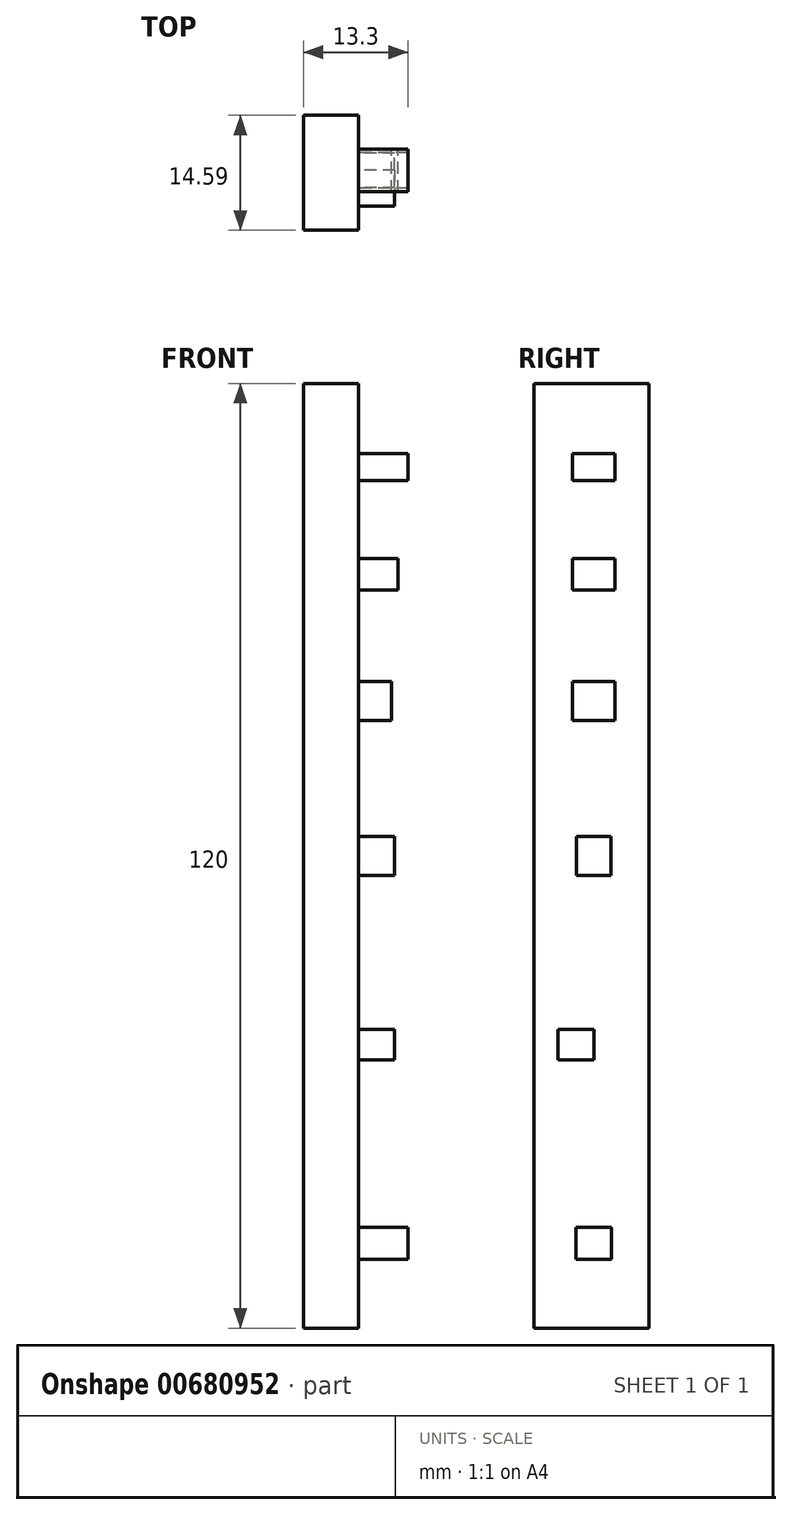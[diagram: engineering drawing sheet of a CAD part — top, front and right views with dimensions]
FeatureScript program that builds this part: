
annotation { "Feature Type Name" : "Feature", "Feature Type Description" : "" }
export const myFeature = defineFeature(function(context is Context, id is Id, definition is map)
    precondition{}
    {
        {
            var Q0;
            Q0=qCreatedBy(makeId("Top.planeOp"),FACE);
            var sketch = newSketch(context, id + "F0", { "sketchPlane" : qUnion([Q0])});
            skLineSegment(sketch, "E0.top", {"start": v(-9.04, 7) * mm, "end": v(-16.04, 7) * mm});
            skLineSegment(sketch, "E0.left", {"start": v(-9.04, 0) * mm, "end": v(-9.04, 7) * mm});
            skLineSegment(sketch, "E0.right", {"start": v(-16.04, 0) * mm, "end": v(-16.04, 7) * mm});
            skLineSegment(sketch, "E1.left", {"start": v(-16.04, 0) * mm, "end": v(-16.04, 0) * mm});
            skLineSegment(sketch, "E1.right", {"start": v(-9.04, 0) * mm, "end": v(-9.04, 0) * mm});
            skLineSegment(sketch, "E2.top", {"start": v(-16.04, -7.6) * mm, "end": v(-9.04, -7.6) * mm});
            skLineSegment(sketch, "E2.left", {"start": v(-16.04, 0) * mm, "end": v(-16.04, -7.6) * mm});
            skLineSegment(sketch, "E2.right", {"start": v(-9.04, 0) * mm, "end": v(-9.04, -7.6) * mm});
            skSolve(sketch);
        }
        {
            var Q0;
            Q0=makeQuery(id+"F0.imprint","IMPRINT",FACE,{"disambiguationData":[TD([[makeQuery(id+"F0.imprint","IMPRINT",EDGE,{"derivedFrom":sQuery(id+"F0.wireOp",EDGE,"E0.top")}),1.0]])]});
            extrude(context, id + "F1", {"entities" : qUnion([Q0]), "endBound" : BoundingType.SYMMETRIC, "depth" : 120 * mm, "offsetDistance" : 25 * mm});
        }
        {
            var Q0;
            Q0=makeQuery(id+"F1.opExtrude","SWEPT_FACE",FACE,{"disambiguationData":[OSD([sQuery(id+"F0.wireOp",EDGE,"E0.left"),sQuery(id+"F0.wireOp",EDGE,"E2.right")])]});
            var sketch = newSketch(context, id + "F2", { "sketchPlane" : qUnion([Q0])});
            skLineSegment(sketch, "E3.bottom", {"start": v(2.26, -51.26) * mm, "end": v(-2.26, -51.26) * mm});
            skLineSegment(sketch, "E3.top", {"start": v(2.26, -47.2) * mm, "end": v(-2.26, -47.2) * mm});
            skLineSegment(sketch, "E3.left", {"start": v(2.26, -51.26) * mm, "end": v(2.26, -47.2) * mm});
            skLineSegment(sketch, "E3.right", {"start": v(-2.26, -51.26) * mm, "end": v(-2.26, -47.2) * mm});
            skPoint(sketch, "E3.middle", {"position": v(0, -49.23) * mm});
            skLineSegment(sketch, "E4.bottom", {"start": v(0, -25.91) * mm, "end": v(-4.53, -25.91) * mm});
            skLineSegment(sketch, "E4.top", {"start": v(0, -22.02) * mm, "end": v(-4.53, -22.02) * mm});
            skLineSegment(sketch, "E4.left", {"start": v(0, -25.91) * mm, "end": v(0, -22.02) * mm});
            skLineSegment(sketch, "E4.right", {"start": v(-4.53, -25.91) * mm, "end": v(-4.53, -22.02) * mm});
            skPoint(sketch, "E4.middle", {"position": v(-2.26, -23.97) * mm});
            skPoint(sketch, "E4.middle.positionSnap0", {"position": v(-2.26, -49.23) * mm});
            skPoint(sketch, "E4.cornerSnap0", {"position": v(0, -51.26) * mm});
            skPoint(sketch, "E4.centerSnap0", {"position": v(-2.26, -49.23) * mm});
            skLineSegment(sketch, "E5.bottom", {"start": v(-2.18, 2.46) * mm, "end": v(2.18, 2.46) * mm});
            skLineSegment(sketch, "E5.top", {"start": v(-2.18, -2.46) * mm, "end": v(2.18, -2.46) * mm});
            skLineSegment(sketch, "E5.left", {"start": v(-2.18, 2.46) * mm, "end": v(-2.18, -2.46) * mm});
            skLineSegment(sketch, "E5.right", {"start": v(2.18, 2.46) * mm, "end": v(2.18, -2.46) * mm});
            skPoint(sketch, "E5.middle", {"position": v(0, 0) * mm});
            skLineSegment(sketch, "E6.bottom", {"start": v(-2.72, 22.18) * mm, "end": v(2.72, 22.18) * mm});
            skLineSegment(sketch, "E6.top", {"start": v(-2.72, 17.18) * mm, "end": v(2.72, 17.18) * mm});
            skLineSegment(sketch, "E6.left", {"start": v(-2.72, 22.18) * mm, "end": v(-2.72, 17.18) * mm});
            skLineSegment(sketch, "E6.right", {"start": v(2.72, 22.18) * mm, "end": v(2.72, 17.18) * mm});
            skPoint(sketch, "E6.middle", {"position": v(0, 19.68) * mm});
            skLineSegment(sketch, "E7.bottom", {"start": v(-2.72, 37.8) * mm, "end": v(2.72, 37.8) * mm});
            skLineSegment(sketch, "E7.top", {"start": v(-2.72, 33.78) * mm, "end": v(2.72, 33.78) * mm});
            skLineSegment(sketch, "E7.left", {"start": v(-2.72, 37.8) * mm, "end": v(-2.72, 33.78) * mm});
            skLineSegment(sketch, "E7.right", {"start": v(2.72, 37.8) * mm, "end": v(2.72, 33.78) * mm});
            skPoint(sketch, "E7.middle", {"position": v(0, 35.79) * mm});
            skLineSegment(sketch, "E8.bottom", {"start": v(-2.72, 51.12) * mm, "end": v(2.72, 51.12) * mm});
            skLineSegment(sketch, "E8.top", {"start": v(-2.72, 47.71) * mm, "end": v(2.72, 47.71) * mm});
            skLineSegment(sketch, "E8.left", {"start": v(-2.72, 51.12) * mm, "end": v(-2.72, 47.71) * mm});
            skLineSegment(sketch, "E8.right", {"start": v(2.72, 51.12) * mm, "end": v(2.72, 47.71) * mm});
            skPoint(sketch, "E8.middle", {"position": v(0, 49.42) * mm});
            skSolve(sketch);
        }
        {
            var Q0;
            Q0=makeQuery(id+"F2.imprint","IMPRINT",FACE,{"disambiguationData":[TD([[makeQuery(id+"F2.imprint","IMPRINT",EDGE,{"derivedFrom":sQuery(id+"F2.wireOp",EDGE,"E8.bottom")}),-1.0]])]});
            var Q1;
            Q1=makeQuery(id+"F2.imprint","IMPRINT",FACE,{"disambiguationData":[TD([[makeQuery(id+"F2.imprint","IMPRINT",EDGE,{"derivedFrom":sQuery(id+"F2.wireOp",EDGE,"E3.bottom")}),-1.0]])]});
            extrude(context, id + "F3", {"entities" : qUnion([Q0, Q1]), "operationType" : NewBodyOperationType.ADD, "depth" : 6.3 * mm, "offsetDistance" : 25 * mm});
        }
        {
            var Q0;
            Q0=makeQuery(id+"F2.imprint","IMPRINT",FACE,{"disambiguationData":[TD([[makeQuery(id+"F2.imprint","IMPRINT",EDGE,{"derivedFrom":sQuery(id+"F2.wireOp",EDGE,"E6.bottom")}),-1.0]])]});
            extrude(context, id + "F4", {"entities" : qUnion([Q0]), "operationType" : NewBodyOperationType.ADD, "depth" : 4.2 * mm, "offsetDistance" : 25 * mm});
        }
        {
            var Q0;
            Q0=makeQuery(id+"F2.imprint","IMPRINT",FACE,{"disambiguationData":[TD([[makeQuery(id+"F2.imprint","IMPRINT",EDGE,{"derivedFrom":sQuery(id+"F2.wireOp",EDGE,"E7.bottom")}),-1.0]])]});
            extrude(context, id + "F5", {"entities" : qUnion([Q0]), "operationType" : NewBodyOperationType.ADD, "depth" : 5 * mm, "offsetDistance" : 25 * mm});
        }
        {
            var Q0;
            Q0=makeQuery(id+"F2.imprint","IMPRINT",FACE,{"disambiguationData":[TD([[makeQuery(id+"F2.imprint","IMPRINT",EDGE,{"derivedFrom":sQuery(id+"F2.wireOp",EDGE,"E5.bottom")}),-1.0]])]});
            extrude(context, id + "F6", {"entities" : qUnion([Q0]), "operationType" : NewBodyOperationType.ADD, "depth" : 4.6 * mm, "offsetDistance" : 25 * mm});
        }
        {
            var Q0;
            Q0=makeQuery(id+"F2.imprint","IMPRINT",FACE,{"disambiguationData":[TD([[makeQuery(id+"F2.imprint","IMPRINT",EDGE,{"derivedFrom":sQuery(id+"F2.wireOp",EDGE,"E4.bottom")}),-1.0]])]});
            extrude(context, id + "F7", {"entities" : qUnion([Q0]), "operationType" : NewBodyOperationType.ADD, "depth" : 4.6 * mm, "offsetDistance" : 25 * mm});
        }
    });
